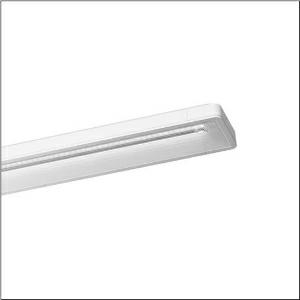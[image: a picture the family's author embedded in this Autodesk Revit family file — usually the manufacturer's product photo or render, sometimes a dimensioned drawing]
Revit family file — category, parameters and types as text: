
# Revit family: taris_r__21_5mt217704wd_5e77
name_source: partatom
category: Lighting Fixtures
units: mm (PartAtom-declared; Revit-internal decimal feet)

## family parameters
Cut with Voids When Loaded = No
Host = Face
Light Source = No
Part Type = Normal
Room Calculation Point = No
Round Connector Dimension = Use Diameter
Shared = No

## types (1)
- Taris® 21 (1 x LED, 6140 lm, 37 W, 4000K)
    Apparent Load = 37 VA
    CIE Flux Codes = 73 96 99 100 100
    Color Rendering = 80
    Color Temperature = 4000K
    Default Elevation = 1800 mm
    Description = Taris® 21, office luminaire, primary anti-glare with micro louvre, primary optical cover: axial lens, of PMMA, structured, CAT 2 (L<= 1500cd/m²), light emission: direct distribution, primary light characteristic: symmetric, installation type: surface-mounted, LED rated luminous flux: 6.140 lm, light colour: 840, colour temperature: 4000K, control gear: ECG, with terminal, 5-pole, mains connection: 230V, AC, 50Hz, rated input power: 37W, housing, luminaire housing, of plastic, traffic white (RAL 9016), length: 1.510 mm, width: 134 mm, height: 50mm, protection rating (complete): IP20, insulation class (complete): insulation class I (protective earthing), certification: CE, ENEC, VDE, protection symbol: F, impact resistance: IK02, permissible ambient temperature for indoor applications: 0..+35°C, standard: EN 50419, packaging unit: 1 piece
    Height = 51 mm
    Lamp = 1 x LED
    Lamp Light Flux = 6140 lm
    Lamp Power = 37 W
    Lamp count = 1
    Length = 1514 mm
    Luminous efficacy = 166 lm/W
    Manufacturer = Siteco
    ModVariant = No
    Model = 5MT217704WD
    Mounting Place = Ceiling
    Mounting Type = Surface mounted
    Number of Poles = 1
    OnlyDefault = Yes
    Power Factor = 1
    Product Name = Taris® 21
    Product group = office luminaire | ceiling mounted
    ProductGroupID = 302
    Protection Class = Protection class I
    Protection Degree = IP 20
    RLX_Detail_Level = 1
    RlxData = <blob elided: 38925 chars, md5=0452bd5e>
    Socket = socket
    Standby Power = 0 W
    System Light Flux = 6140 lm
    System Power = 37 W
    Type Comments = Product without accessories
    Type Image = l_1004728.jpg
    URL = http://relux.com
    VarID = ---
    Voltage = 0 V
    Weight = 0.00 kg
    Width = 134 mm

## geometry (parser evidence)
native form markers: Blend x4, Sweep x9
no freeform markers — native parametric forms only
